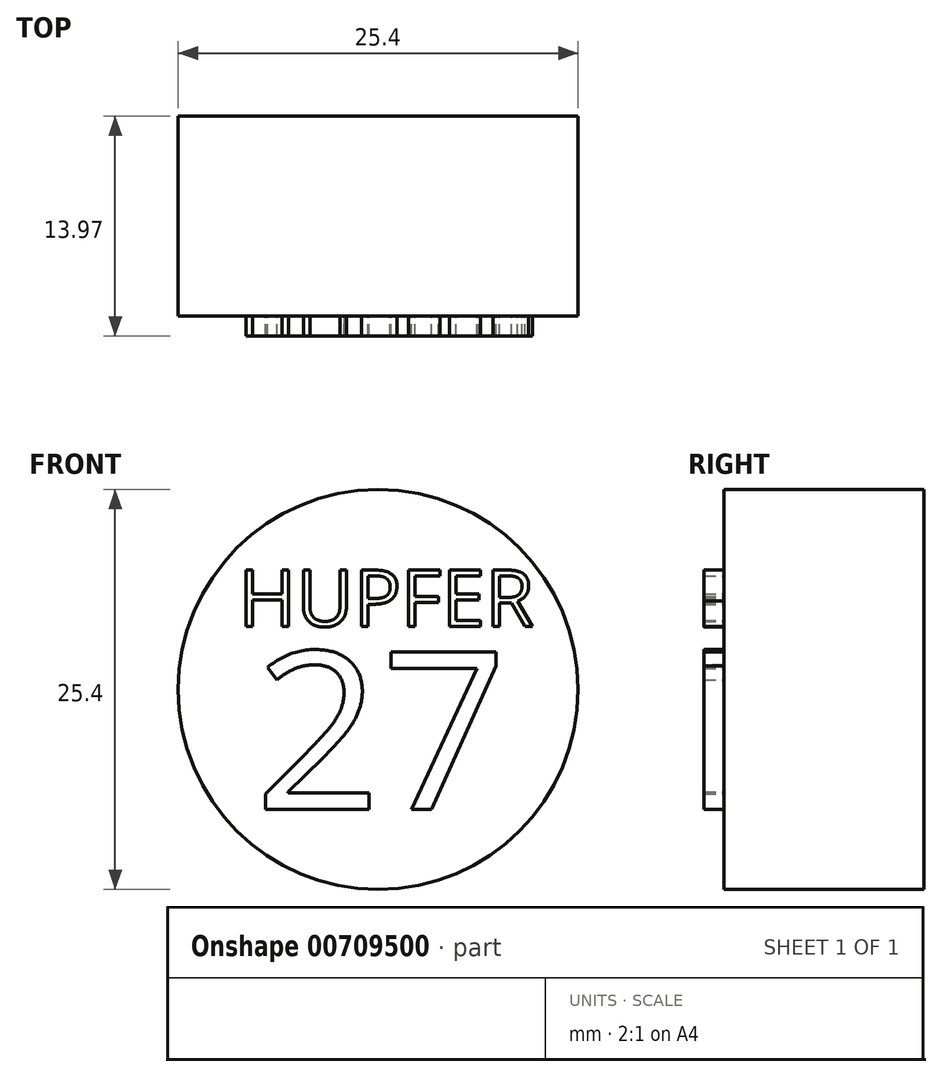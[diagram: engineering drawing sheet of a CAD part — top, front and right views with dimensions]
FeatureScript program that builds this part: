
annotation { "Feature Type Name" : "Feature", "Feature Type Description" : "" }
export const myFeature = defineFeature(function(context is Context, id is Id, definition is map)
    precondition{}
    {
        {
            var Q0;
            Q0=qCreatedBy(makeId("Front.planeOp"),FACE);
            var sketch = newSketch(context, id + "F0", { "sketchPlane" : qUnion([Q0])});
            skCircle(sketch, "E0", {"center": v(-15.19, 33.24) * mm, "radius": 12.7 * mm});
            skSolve(sketch);
        }
        {
            var Q0;
            Q0 = qSketchRegion(id + "F0", true);
            extrude(context, id + "F1", {"entities" : qUnion([Q0]), "depth" : 12.7 * mm, "offsetDistance" : 25.4 * mm});
        }
        {
            var Q0;
            Q0=makeQuery(id+"F1.opExtrude","CAP_FACE",FACE,{"disambiguationData":[OSD([sQuery(id+"F0.wireOp",EDGE,"E0")])],"isStart":false});
            var sketch = newSketch(context, id + "F2", { "sketchPlane" : qUnion([Q0])});
            skText(sketch, "E1", { "text": "HUPFER", "fontName": "OpenSans-Regular.ttf"});
            const initialGuessF2  = {"E1": [-0.02408, 0.03725, 1, 0, 0.0036]};
            skSetInitialGuess(sketch, initialGuessF2);
            skSolve(sketch);
        }
        {
            var Q0;
            Q0 = qSketchRegion(id + "F2", true);
            extrude(context, id + "F3", {"entities" : qUnion([Q0]), "operationType" : NewBodyOperationType.ADD, "depth" : 1.27 * mm, "offsetDistance" : 25.4 * mm});
        }
        {
            var Q0;
            {var subQ0=sQuery(id+"F0.wireOp",EDGE,"E0");Q0=makeQuery(id+"F3.boolean.opBoolean","SPLIT",FACE,{"disambiguationData":[TD([makeQuery(id+"F1.opExtrude","SWEPT_FACE",FACE,{"disambiguationData":[OSD([subQ0])]})])],"derivedFrom":makeQuery(id+"F1.opExtrude","CAP_FACE",FACE,{"disambiguationData":[OSD([subQ0])],"isStart":false})});}
            var sketch = newSketch(context, id + "F4", { "sketchPlane" : qUnion([Q0])});
            skText(sketch, "E2", { "text": "27", "fontName": "OpenSans-Regular.ttf"});
            const initialGuessF4  = {"E2": [-0.02304, 0.02562, 1, 0, 0.0101]};
            skSetInitialGuess(sketch, initialGuessF4);
            skSolve(sketch);
        }
        {
            var Q0;
            Q0 = qSketchRegion(id + "F4", true);
            extrude(context, id + "F5", {"entities" : qUnion([Q0]), "operationType" : NewBodyOperationType.ADD, "depth" : 1.27 * mm, "offsetDistance" : 25.4 * mm});
        }
    });
